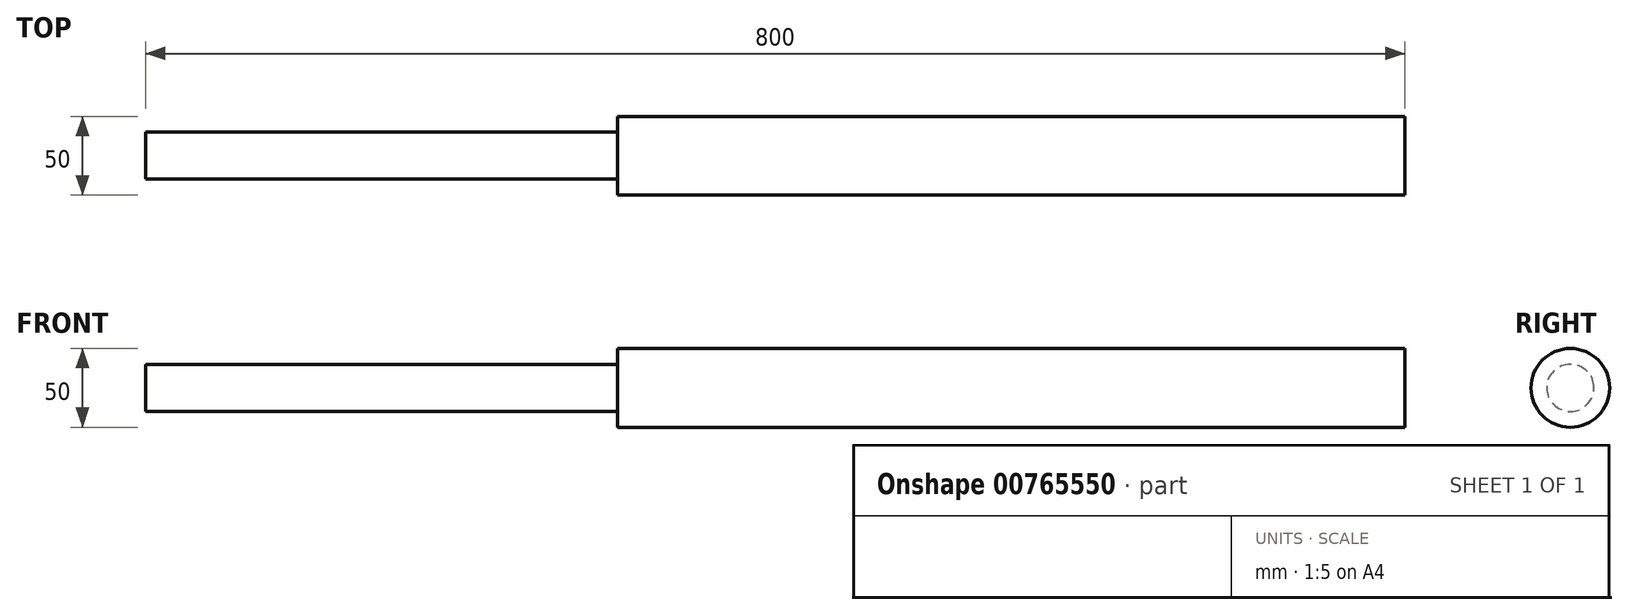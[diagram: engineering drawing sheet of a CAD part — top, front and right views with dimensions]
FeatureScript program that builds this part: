
annotation { "Feature Type Name" : "Feature", "Feature Type Description" : "" }
export const myFeature = defineFeature(function(context is Context, id is Id, definition is map)
    precondition{}
    {
        {
            var Q0;
            Q0=qCreatedBy(makeId("Right.planeOp"),FACE);
            var sketch = newSketch(context, id + "F0", { "sketchPlane" : qUnion([Q0])});
            skCircle(sketch, "E0", {"center": v(0, 6.9) * mm, "radius": 25 * mm});
            skSolve(sketch);
        }
        {
            var Q0;
            Q0 = qSketchRegion(id + "F0", true);
            extrude(context, id + "F1", {"entities" : qUnion([Q0]), "depth" : 500 * mm, "offsetDistance" : 25.4 * mm});
        }
        {
            var Q0;
            Q0=makeQuery(id+"F1.opExtrude","CAP_FACE",FACE,{"disambiguationData":[OSD([sQuery(id+"F0.wireOp",EDGE,"E0")])],"isStart":true});
            var sketch = newSketch(context, id + "F2", { "sketchPlane" : qUnion([Q0])});
            skCircle(sketch, "E1", {"center": v(0, 6.9) * mm, "radius": 15 * mm});
            skSolve(sketch);
        }
        {
            var Q0;
            Q0 = qSketchRegion(id + "F2", true);
            var Q1;
            Q1=makeQuery(id+"F2.imprint","IMPRINT",FACE,{"disambiguationData":[TD([[makeQuery(id+"F2.imprint","IMPRINT",EDGE,{"derivedFrom":sQuery(id+"F2.wireOp",EDGE,"E1")}),1.0]])]});
            extrude(context, id + "F3", {"entities" : qUnion([Q0, Q1]), "operationType" : NewBodyOperationType.ADD, "depth" : 300 * mm, "offsetDistance" : 25.4 * mm});
        }
    });
